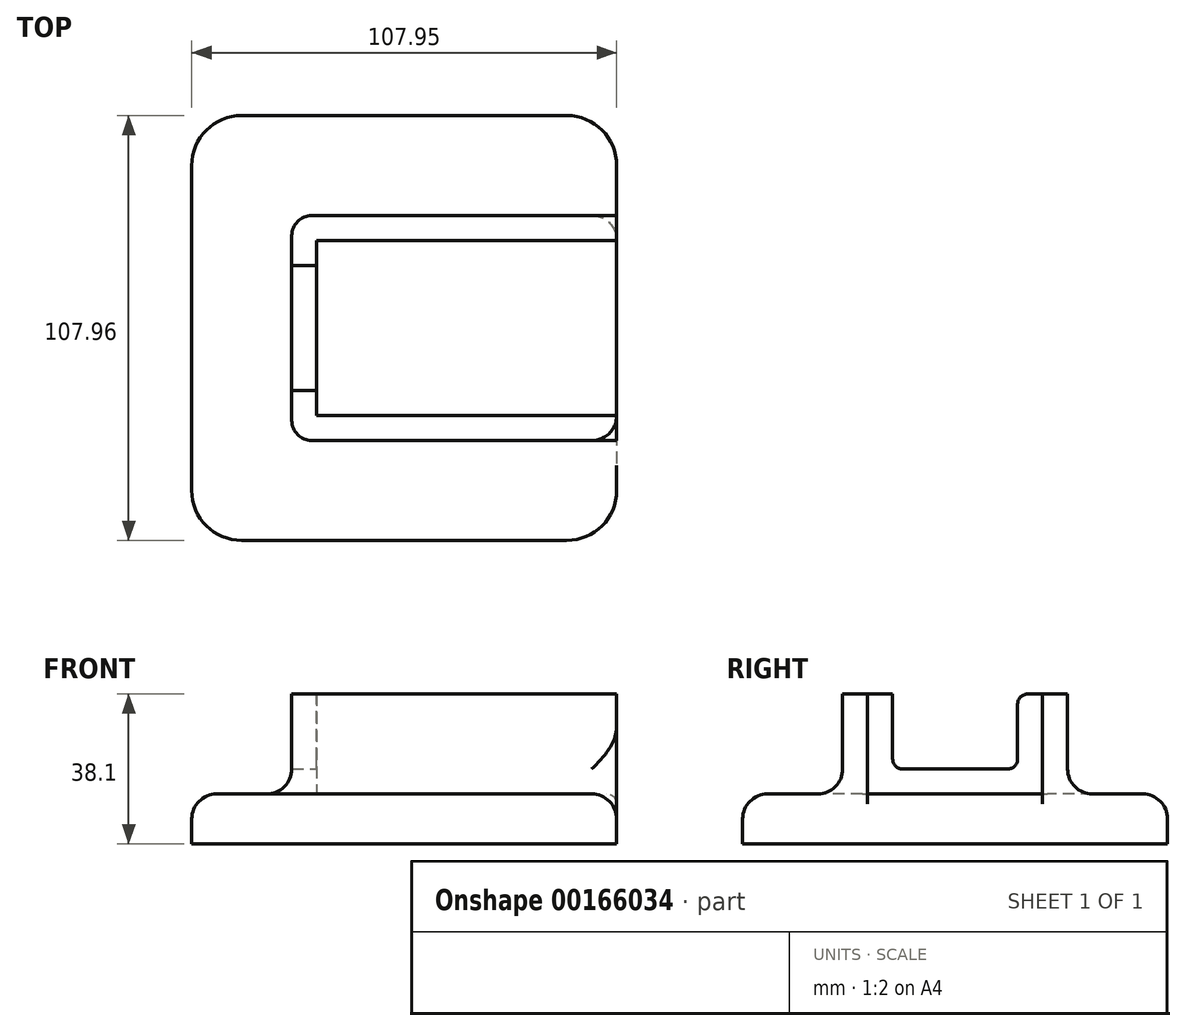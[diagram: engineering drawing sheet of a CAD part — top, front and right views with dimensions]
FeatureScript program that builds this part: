
annotation { "Feature Type Name" : "Feature", "Feature Type Description" : "" }
export const myFeature = defineFeature(function(context is Context, id is Id, definition is map)
    precondition{}
    {
        {
            var Q0;
            Q0=qCreatedBy(makeId("Top.planeOp"),FACE);
            var sketch = newSketch(context, id + "F0", { "sketchPlane" : qUnion([Q0])});
            skLineSegment(sketch, "E0.bottom", {"start": v(-45.16, 22.23) * mm, "end": v(31.04, 22.23) * mm});
            skLineSegment(sketch, "E0.top", {"start": v(-45.16, -22.23) * mm, "end": v(31.04, -22.23) * mm});
            skLineSegment(sketch, "E0.left", {"start": v(-45.16, 22.23) * mm, "end": v(-45.16, -22.23) * mm});
            skLineSegment(sketch, "E0.right", {"start": v(31.04, 22.23) * mm, "end": v(31.04, -22.23) * mm, "construction": true});
            skLineSegment(sketch, "E1.bottom", {"start": v(31.04, -28.57) * mm, "end": v(-51.51, -28.58) * mm});
            skLineSegment(sketch, "E1.top", {"start": v(31.04, 28.58) * mm, "end": v(-51.51, 28.57) * mm});
            skLineSegment(sketch, "E1.left", {"start": v(31.04, -28.57) * mm, "end": v(31.04, 28.58) * mm});
            skLineSegment(sketch, "E1.right", {"start": v(-51.51, -28.58) * mm, "end": v(-51.51, 28.57) * mm});
            skSolve(sketch);
        }
        {
            var Q0;
            {var subQ2=sQuery(id+"F0.wireOp",EDGE,"E0.bottom");Q0=makeQuery(id+"F0.imprint","IMPRINT",FACE,{"disambiguationData":[TD([[makeQuery(id+"F0.imprint","IMPRINT",EDGE,{"derivedFrom":subQ2}),1.0]])]});}
            extrude(context, id + "F1", {"entities" : qUnion([Q0]), "depth" : 25.4 * mm});
        }
        {
            var Q0;
            Q0=qCreatedBy(makeId("Top.planeOp"),FACE);
            var sketch = newSketch(context, id + "F2", { "sketchPlane" : qUnion([Q0])});
            skLineSegment(sketch, "E2.bottom", {"start": v(31.04, -53.98) * mm, "end": v(-76.91, -53.98) * mm});
            skLineSegment(sketch, "E2.top", {"start": v(31.04, 53.98) * mm, "end": v(-76.91, 53.98) * mm});
            skLineSegment(sketch, "E2.left", {"start": v(31.04, -53.98) * mm, "end": v(31.04, 53.98) * mm});
            skLineSegment(sketch, "E2.right", {"start": v(-76.91, -53.98) * mm, "end": v(-76.91, 53.98) * mm});
            skLineSegment(sketch, "E3", {"start": v(-51.51, -3.7) * mm, "end": v(-76.91, -3.7) * mm, "construction": true});
            skLineSegment(sketch, "E4", {"start": v(-32.96, 53.98) * mm, "end": v(-32.96, 28.57) * mm, "construction": true});
            skSolve(sketch);
        }
        {
            var Q0;
            Q0=makeQuery(id+"F2.imprint","IMPRINT",FACE,{"disambiguationData":[TD([[makeQuery(id+"F2.imprint","IMPRINT",EDGE,{"derivedFrom":sQuery(id+"F2.wireOp",EDGE,"E2.bottom")}),-1.0]])]});
            extrude(context, id + "F3", {"entities" : qUnion([Q0]), "operationType" : NewBodyOperationType.ADD, "oppositeDirection" : true, "depth" : 12.7 * mm});
        }
        {
            var Q0;
            Q0=makeQuery(id+"F3.opExtrude","SWEPT_EDGE",EDGE,{"disambiguationData":[OSD([sQuery(id+"F2.wireOp",EDGE,"E2.bottom"),sQuery(id+"F2.wireOp",EDGE,"E2.right")])]});
            var Q1;
            Q1=makeQuery(id+"F3.opExtrude","SWEPT_EDGE",EDGE,{"disambiguationData":[OSD([sQuery(id+"F2.wireOp",EDGE,"E2.top"),sQuery(id+"F2.wireOp",EDGE,"E2.right")])]});
            var Q2;
            Q2=makeQuery(id+"F3.opExtrude","SWEPT_EDGE",EDGE,{"disambiguationData":[OSD([sQuery(id+"F2.wireOp",EDGE,"E2.bottom"),sQuery(id+"F2.wireOp",EDGE,"E2.left")])]});
            var Q3;
            Q3=makeQuery(id+"F3.opExtrude","SWEPT_EDGE",EDGE,{"disambiguationData":[OSD([sQuery(id+"F2.wireOp",EDGE,"E2.top"),sQuery(id+"F2.wireOp",EDGE,"E2.left")])]});
            fillet(context, id + "F4", {"entities" : qUnion([Q0, Q1, Q2, Q3]), "radius" : 12.7 * mm, "tangentPropagation" : true, "allowEdgeOverflow" : false});
        }
        {
            var Q0;
            Q0=makeQuery(id+"F1.opExtrude","SWEPT_EDGE",EDGE,{"disambiguationData":[OSD([sQuery(id+"F0.wireOp",EDGE,"E1.bottom"),sQuery(id+"F0.wireOp",EDGE,"E1.right")])]});
            var Q1;
            Q1=makeQuery(id+"F1.opExtrude","SWEPT_EDGE",EDGE,{"disambiguationData":[OSD([sQuery(id+"F0.wireOp",EDGE,"E1.top"),sQuery(id+"F0.wireOp",EDGE,"E1.right")])]});
            fillet(context, id + "F5", {"entities" : qUnion([Q0, Q1]), "radius" : 5.08 * mm, "tangentPropagation" : true, "allowEdgeOverflow" : false});
        }
        {
            var Q0;
            {var subQ2=sQuery(id+"F2.wireOp",EDGE,"E2.right");var subQ3=sQuery(id+"F0.wireOp",EDGE,"E1.bottom");var subQ4=sQuery(id+"F2.wireOp",EDGE,"E2.bottom");var subQ5=sQuery(id+"F2.wireOp",EDGE,"E2.top");var subQ6=sQuery(id+"F2.wireOp",EDGE,"E2.left");Q0=makeQuery(id+"F3.boolean.opBoolean","SPLIT",FACE,{"disambiguationData":[TD([makeQuery(id+"F1.opExtrude","SWEPT_FACE",FACE,{"disambiguationData":[OSD([subQ3])]})])],"derivedFrom":makeQuery(id+"F3.opExtrude","CAP_FACE",FACE,{"disambiguationData":[OSD([subQ4,subQ5,subQ6,subQ2])],"isStart":true})});}
            fillet(context, id + "F6", {"entities" : qUnion([Q0]), "radius" : 6.35 * mm, "tangentPropagation" : true, "allowEdgeOverflow" : false});
        }
        {
            var Q0;
            Q0=makeQuery(id+"F1.opExtrude","CAP_FACE",FACE,{"disambiguationData":[OSD([sQuery(id+"F0.wireOp",EDGE,"E0.bottom"),sQuery(id+"F0.wireOp",EDGE,"E0.top"),sQuery(id+"F0.wireOp",EDGE,"E0.left"),sQuery(id+"F0.wireOp",EDGE,"E1.bottom"),sQuery(id+"F0.wireOp",EDGE,"E1.top"),sQuery(id+"F0.wireOp",EDGE,"E1.left"),sQuery(id+"F0.wireOp",EDGE,"E1.right")])],"isStart":false});
            var sketch = newSketch(context, id + "F7", { "sketchPlane" : qUnion([Q0])});
            skLineSegment(sketch, "E5", {"start": v(-34.8, 28.57) * mm, "end": v(-34.8, 22.23) * mm, "construction": true});
            skLineSegment(sketch, "E6", {"start": v(-45.16, 22.23) * mm, "end": v(-51.51, 22.23) * mm, "construction": true});
            skLineSegment(sketch, "E7", {"start": v(-45.16, -22.23) * mm, "end": v(-51.51, -22.23) * mm});
            skLineSegment(sketch, "E8.bottom", {"start": v(-51.51, 15.88) * mm, "end": v(-45.16, 15.88) * mm});
            skLineSegment(sketch, "E8.top", {"start": v(-51.51, -15.88) * mm, "end": v(-45.16, -15.88) * mm});
            skLineSegment(sketch, "E8.left", {"start": v(-51.51, 15.88) * mm, "end": v(-51.51, -15.88) * mm});
            skLineSegment(sketch, "E8.right", {"start": v(-45.16, 15.88) * mm, "end": v(-45.16, -15.88) * mm});
            skLineSegment(sketch, "E9", {"start": v(-48.34, 22.23) * mm, "end": v(-48.34, 15.88) * mm, "construction": true});
            skLineSegment(sketch, "E10", {"start": v(-48.34, -22.23) * mm, "end": v(-48.34, -15.88) * mm, "construction": true});
            skSolve(sketch);
        }
        {
            var Q0;
            Q0 = qSketchRegion(id + "F7", true);
            extrude(context, id + "F8", {"entities" : qUnion([Q0]), "operationType" : NewBodyOperationType.REMOVE, "oppositeDirection" : true, "depth" : 19.05 * mm});
        }
        {
            var Q0;
            Q0=makeQuery(id+"F8.boolean.opBoolean","COPY",EDGE,{"derivedFrom":makeQuery(id+"F8.opExtrude","CAP_EDGE",EDGE,{"disambiguationData":[OSD([sQuery(id+"F7.wireOp",EDGE,"E8.bottom")])],"isStart":false})});
            var Q1;
            Q1=makeQuery(id+"F8.boolean.opBoolean","COPY",EDGE,{"derivedFrom":makeQuery(id+"F8.opExtrude","CAP_EDGE",EDGE,{"disambiguationData":[OSD([sQuery(id+"F7.wireOp",EDGE,"E8.bottom")])],"isStart":true})});
            var Q2;
            Q2=makeQuery(id+"F8.boolean.opBoolean","COPY",EDGE,{"derivedFrom":makeQuery(id+"F8.opExtrude","CAP_EDGE",EDGE,{"disambiguationData":[OSD([sQuery(id+"F7.wireOp",EDGE,"E8.top")])],"isStart":true})});
            var Q3;
            Q3=makeQuery(id+"F8.boolean.opBoolean","COPY",EDGE,{"derivedFrom":makeQuery(id+"F8.opExtrude","CAP_EDGE",EDGE,{"disambiguationData":[OSD([sQuery(id+"F7.wireOp",EDGE,"E8.top")])],"isStart":false})});
            var Q4;
            {var subQ2=sQuery(id+"F0.wireOp",EDGE,"E0.bottom");var subQ3=sQuery(id+"F2.wireOp",EDGE,"E2.left");Q4=makeQuery(id+"F3.boolean.opBoolean","SPLIT",EDGE,{"disambiguationData":[TD([makeQuery(id+"F1.opExtrude","SWEPT_FACE",FACE,{"disambiguationData":[OSD([subQ2])]})])],"derivedFrom":makeQuery(id+"F3.opExtrude","CAP_EDGE",EDGE,{"disambiguationData":[OSD([subQ3])],"isStart":true})});}
            var Q5;
            Q5=makeQuery(id+"F6.opFillet","BLEND_EDGE",EDGE,{"blendedFrom":[makeQuery(id+"F1.opExtrude","SWEPT_EDGE",EDGE,{"disambiguationData":[OSD([sQuery(id+"F0.wireOp",EDGE,"E1.top"),sQuery(id+"F0.wireOp",EDGE,"E1.left")])]}),makeQuery(id+"F1.opExtrude","SWEPT_FACE",FACE,{"disambiguationData":[OSD([sQuery(id+"F0.wireOp",EDGE,"E0.bottom")])]})],"blendedInto":[makeQuery(id+"F1.opExtrude","SWEPT_FACE",FACE,{"disambiguationData":[OSD([sQuery(id+"F0.wireOp",EDGE,"E0.bottom")])]})]});
            var Q6;
            Q6=makeQuery(id+"F6.opFillet","BLEND_EDGE",EDGE,{"blendedFrom":[makeQuery(id+"F1.opExtrude","SWEPT_EDGE",EDGE,{"disambiguationData":[OSD([sQuery(id+"F0.wireOp",EDGE,"E1.bottom"),sQuery(id+"F0.wireOp",EDGE,"E1.left")])]}),makeQuery(id+"F1.opExtrude","SWEPT_FACE",FACE,{"disambiguationData":[OSD([sQuery(id+"F0.wireOp",EDGE,"E0.top")])]})],"blendedInto":[makeQuery(id+"F1.opExtrude","SWEPT_FACE",FACE,{"disambiguationData":[OSD([sQuery(id+"F0.wireOp",EDGE,"E0.top")])]})]});
            fillet(context, id + "F9", {"entities" : qUnion([Q0, Q1, Q2, Q3, Q4, Q5, Q6]), "radius" : 2.54 * mm, "tangentPropagation" : true, "allowEdgeOverflow" : false});
        }
    });
